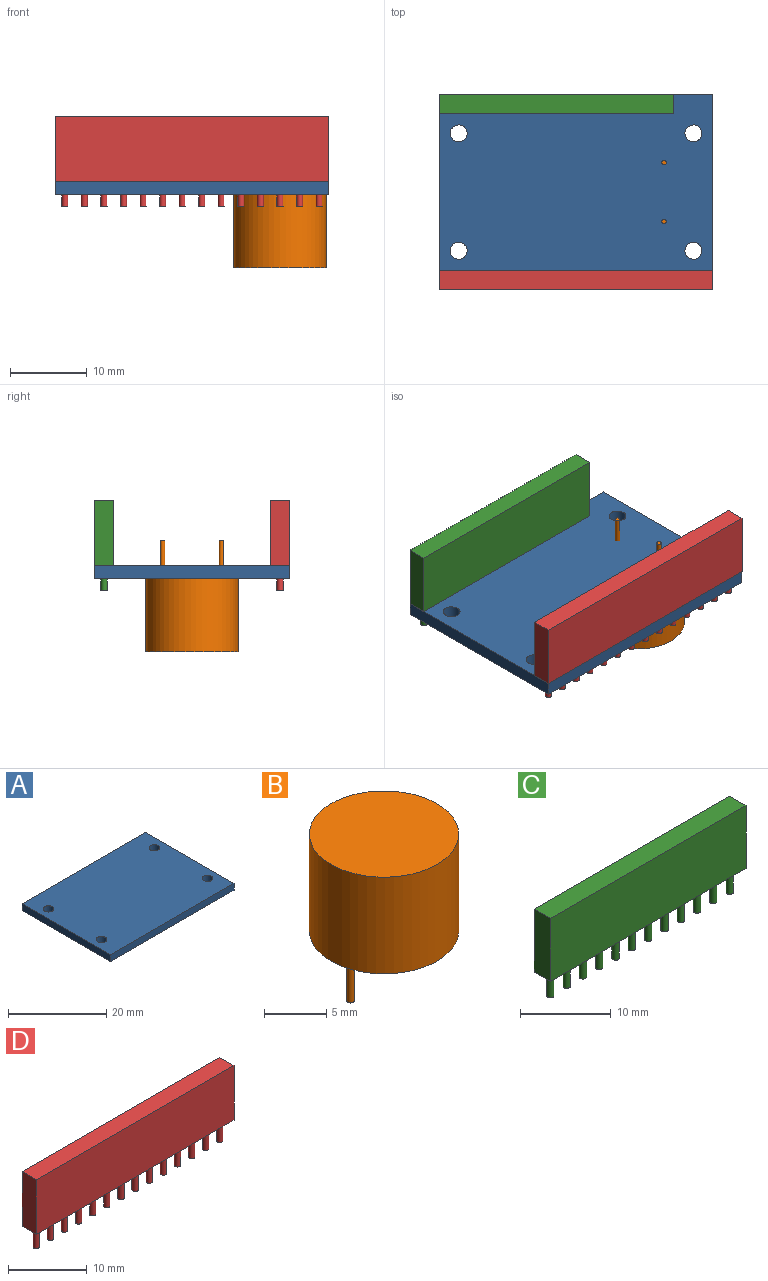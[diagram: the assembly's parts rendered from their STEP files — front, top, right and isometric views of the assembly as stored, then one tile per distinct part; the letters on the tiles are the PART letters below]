
ASSEMBLY  parts=4 mates=3
PART A: 10 faces, bbox 35.6x25.4x1.7 mm
  f0: plane 25.4x1.7mm, normal (1,0,0), area 43.2mm2, adj f1,f6,f8,f9
  f1: plane 35.56x1.7mm, normal (0,1,0), area 60.5mm2, adj f0,f2,f8,f9
  f2: plane 25.4x1.7mm, normal (-1,0,0), area 43.2mm2, adj f1,f6,f8,f9
  f3: cylinder r=1.1mm len=2.2mm, axis (0,0,1), area 11.7mm2, adj f8,f9
  f4: cylinder r=1.1mm len=2.2mm, axis (0,0,1), area 11.7mm2, adj f8,f9
  f5: cylinder r=1.1mm len=2.2mm, axis (0,0,1), area 11.7mm2, adj f8,f9
  f6: plane 35.56x1.7mm, normal (0,-1,0), area 60.5mm2, adj f0,f2,f8,f9
  f7: cylinder r=1.1mm len=2.2mm, axis (0,0,1), area 11.7mm2, adj f8,f9
  f8: plane 35.56x25.4mm, normal (0,0,-1), area 888mm2, adj f0,f1,f2,f3,f4,f5,f6,f7
  f9: plane 35.56x25.4mm, normal (0,0,1), area 888mm2, adj f0,f1,f2,f3,f4,f5,f6,f7
PART B: 7 faces, bbox 12x12x14.5 mm
  f0: cylinder r=6mm len=12mm, axis (0,0,-1), area 358.1mm2, adj f1,f2
  f1: plane 12x12mm, normal (0,0,1), area 113.1mm2, adj f0
  f2: plane 12x12mm, normal (0,0,-1), area 112.5mm2, adj f0,f3,f5
  f3: cylinder r=0.3mm len=5mm, axis (0,0,1), area 9.4mm2, adj f2,f4
  f4: plane 0.6x0.6mm, normal (0,0,-1), area 0.3mm2, adj f3
  f5: cylinder r=0.3mm len=5mm, axis (0,0,1), area 9.4mm2, adj f2,f6
  f6: plane 0.6x0.6mm, normal (0,0,-1), area 0.3mm2, adj f5
PART C: 30 faces, bbox 30.5x2.6x11.7 mm
  f0: plane 30.49x8.5mm, normal (0,1,0), area 259.2mm2, adj f1,f3,f4,f27
  f1: plane 8.5x2.55mm, normal (-1,0,0), area 21.7mm2, adj f0,f2,f3,f4
  f2: plane 30.49x8.5mm, normal (0,-1,0), area 259.2mm2, adj f1,f3,f4,f27
  f3: plane 30.49x2.55mm, normal (0,0,-1), area 71.7mm2, adj f0,f1,f2,f5,f7,f9,f11,f13
  f4: plane 30.49x2.55mm, normal (0,0,1), area 77.7mm2, adj f0,f1,f2,f27
  f5: cylinder r=0.4mm len=3.2mm, axis (0,0,1), area 8mm2, adj f3,f6
  f6: plane 0.8x0.8mm, normal (0,0,-1), area 0.5mm2, adj f5
  f7: cylinder r=0.4mm len=3.2mm, axis (0,0,1), area 8mm2, adj f3,f8
  f8: plane 0.8x0.8mm, normal (0,0,-1), area 0.5mm2, adj f7
  f9: cylinder r=0.4mm len=3.2mm, axis (0,0,1), area 8mm2, adj f3,f10
  f10: plane 0.8x0.8mm, normal (0,0,-1), area 0.5mm2, adj f9
  f11: cylinder r=0.4mm len=3.2mm, axis (0,0,1), area 8mm2, adj f3,f12
  f12: plane 0.8x0.8mm, normal (0,0,-1), area 0.5mm2, adj f11
  f13: cylinder r=0.4mm len=3.2mm, axis (0,0,1), area 8mm2, adj f3,f14
  f14: plane 0.8x0.8mm, normal (0,0,-1), area 0.5mm2, adj f13
  f15: cylinder r=0.4mm len=3.2mm, axis (0,0,1), area 8mm2, adj f3,f16
  f16: plane 0.8x0.8mm, normal (0,0,-1), area 0.5mm2, adj f15
  f17: cylinder r=0.4mm len=3.2mm, axis (0,0,1), area 8mm2, adj f3,f18
  f18: plane 0.8x0.8mm, normal (0,0,-1), area 0.5mm2, adj f17
  f19: cylinder r=0.4mm len=3.2mm, axis (0,0,1), area 8mm2, adj f3,f20
  f20: plane 0.8x0.8mm, normal (0,0,-1), area 0.5mm2, adj f19
  f21: cylinder r=0.4mm len=3.2mm, axis (0,0,1), area 8mm2, adj f3,f22
  f22: plane 0.8x0.8mm, normal (0,0,-1), area 0.5mm2, adj f21
  f23: cylinder r=0.4mm len=3.2mm, axis (0,0,1), area 8mm2, adj f3,f24
  f24: plane 0.8x0.8mm, normal (0,0,-1), area 0.5mm2, adj f23
  f25: cylinder r=0.4mm len=3.2mm, axis (0,0,1), area 8mm2, adj f3,f26
  f26: plane 0.8x0.8mm, normal (0,0,-1), area 0.5mm2, adj f25
  f27: plane 8.5x2.55mm, normal (1,0,0), area 21.7mm2, adj f0,f2,f3,f4
  f28: cylinder r=0.4mm len=3.2mm, axis (0,0,1), area 8mm2, adj f3,f29
  f29: plane 0.8x0.8mm, normal (0,0,-1), area 0.5mm2, adj f28
PART D: 34 faces, bbox 35.6x2.6x11.7 mm
  f0: plane 35.57x8.5mm, normal (0,1,0), area 302.3mm2, adj f1,f3,f4,f31
  f1: plane 8.5x2.55mm, normal (-1,0,0), area 21.7mm2, adj f0,f2,f3,f4
  f2: plane 35.57x8.5mm, normal (0,-1,0), area 302.3mm2, adj f1,f3,f4,f31
  f3: plane 35.57x2.55mm, normal (0,0,-1), area 83.7mm2, adj f0,f1,f2,f5,f7,f9,f11,f13
  f4: plane 35.57x2.55mm, normal (0,0,1), area 90.7mm2, adj f0,f1,f2,f31
  f5: cylinder r=0.4mm len=3.2mm, axis (0,0,1), area 8mm2, adj f3,f6
  f6: plane 0.8x0.8mm, normal (0,0,-1), area 0.5mm2, adj f5
  f7: cylinder r=0.4mm len=3.2mm, axis (0,0,1), area 8mm2, adj f3,f8
  f8: plane 0.8x0.8mm, normal (0,0,-1), area 0.5mm2, adj f7
  f9: cylinder r=0.4mm len=3.2mm, axis (0,0,1), area 8mm2, adj f3,f10
  f10: plane 0.8x0.8mm, normal (0,0,-1), area 0.5mm2, adj f9
  f11: cylinder r=0.4mm len=3.2mm, axis (0,0,1), area 8mm2, adj f3,f12
  f12: plane 0.8x0.8mm, normal (0,0,-1), area 0.5mm2, adj f11
  f13: cylinder r=0.4mm len=3.2mm, axis (0,0,1), area 8mm2, adj f3,f14
  f14: plane 0.8x0.8mm, normal (0,0,-1), area 0.5mm2, adj f13
  f15: cylinder r=0.4mm len=3.2mm, axis (0,0,1), area 8mm2, adj f3,f16
  f16: plane 0.8x0.8mm, normal (0,0,-1), area 0.5mm2, adj f15
  f17: cylinder r=0.4mm len=3.2mm, axis (0,0,1), area 8mm2, adj f3,f18
  f18: plane 0.8x0.8mm, normal (0,0,-1), area 0.5mm2, adj f17
  f19: cylinder r=0.4mm len=3.2mm, axis (0,0,1), area 8mm2, adj f3,f20
  f20: plane 0.8x0.8mm, normal (0,0,-1), area 0.5mm2, adj f19
  f21: cylinder r=0.4mm len=3.2mm, axis (0,0,1), area 8mm2, adj f3,f22
  f22: plane 0.8x0.8mm, normal (0,0,-1), area 0.5mm2, adj f21
  f23: cylinder r=0.4mm len=3.2mm, axis (0,0,1), area 8mm2, adj f3,f24
  f24: plane 0.8x0.8mm, normal (0,0,-1), area 0.5mm2, adj f23
  f25: cylinder r=0.4mm len=3.2mm, axis (0,0,1), area 8mm2, adj f3,f26
  f26: plane 0.8x0.8mm, normal (0,0,-1), area 0.5mm2, adj f25
  f27: cylinder r=0.4mm len=3.2mm, axis (0,0,1), area 8mm2, adj f3,f28
  f28: plane 0.8x0.8mm, normal (0,0,-1), area 0.5mm2, adj f27
  f29: cylinder r=0.4mm len=3.2mm, axis (0,0,1), area 8mm2, adj f3,f30
  f30: plane 0.8x0.8mm, normal (0,0,-1), area 0.5mm2, adj f29
  f31: plane 8.5x2.55mm, normal (1,0,0), area 21.7mm2, adj f0,f2,f3,f4
  f32: cylinder r=0.4mm len=3.2mm, axis (0,0,1), area 8mm2, adj f3,f33
  f33: plane 0.8x0.8mm, normal (0,0,-1), area 0.5mm2, adj f32
PLACE A at identity fixed
PLACE B rot(axis=(0.71,-0.71,0),180deg) t=(11.43,0,-1.7)mm
PLACE C t=(-16.51,11.43,8.5)mm
PLACE D t=(-16.51,-11.43,8.5)mm
MATE fastened B.f0 <-> A.f8  axis (0,0,1) through (11.43,0,-1.7)mm
MATE fastened C.f5 <-> A.f9  axis (0,0,-1) through (-16.51,11.43,0)mm
MATE fastened A.f9 <-> D.f5  axis (0,0,1) through (-16.51,-11.43,0)mm
